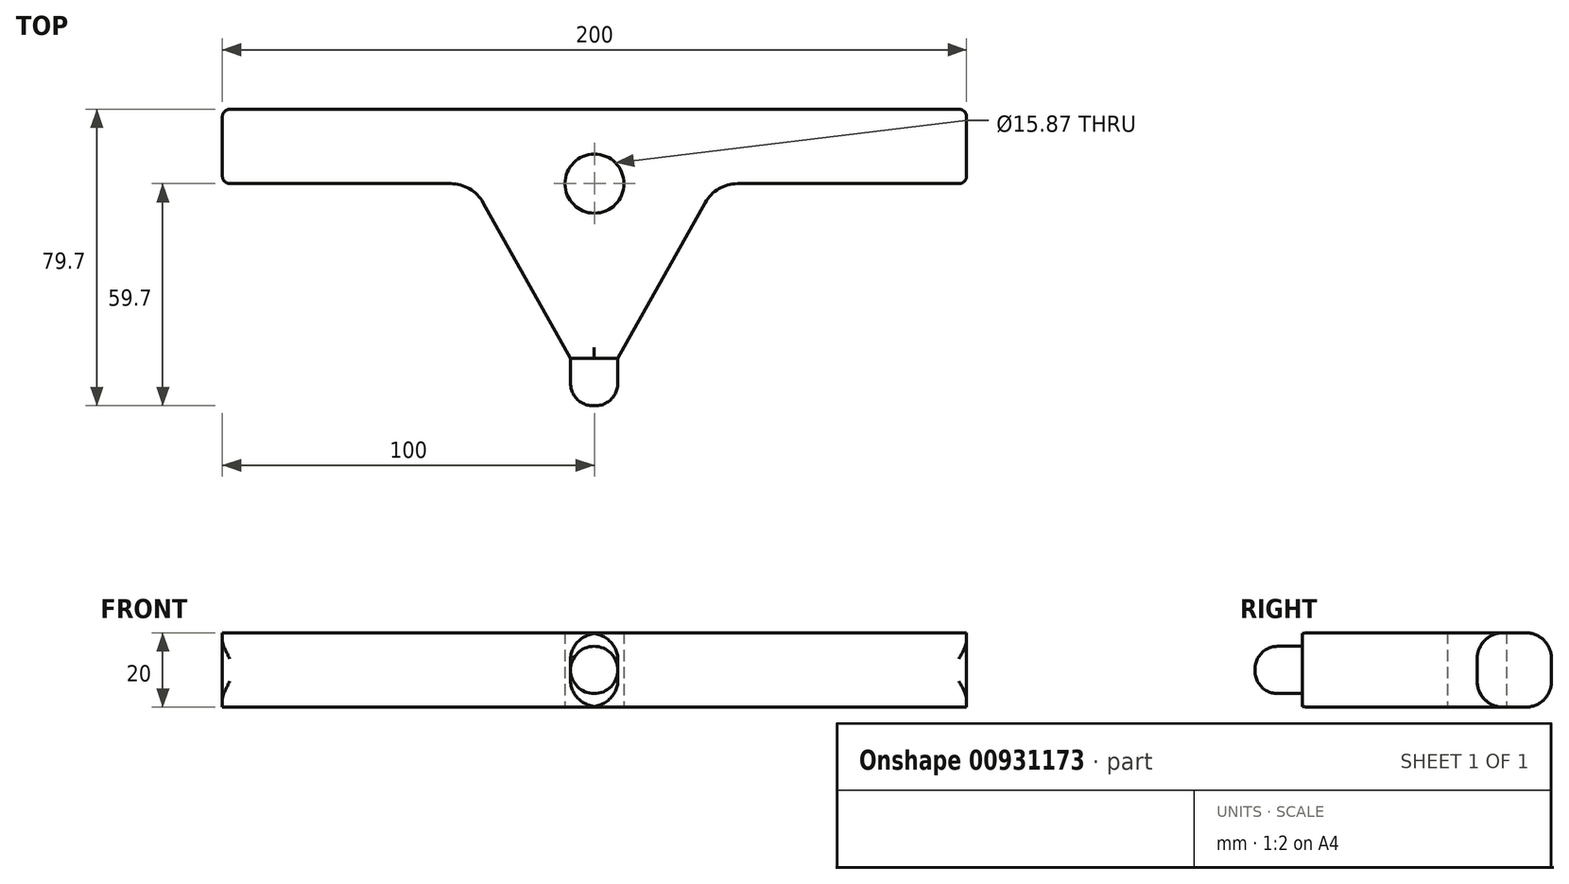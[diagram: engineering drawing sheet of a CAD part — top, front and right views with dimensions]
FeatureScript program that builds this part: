
annotation { "Feature Type Name" : "Feature", "Feature Type Description" : "" }
export const myFeature = defineFeature(function(context is Context, id is Id, definition is map)
    precondition{}
    {
        {
            var Q0;
            Q0=qCreatedBy(makeId("Top.planeOp"),FACE);
            var sketch = newSketch(context, id + "F0", { "sketchPlane" : qUnion([Q0])});
            skLineSegment(sketch, "E0.top", {"start": v(-98, 20) * mm, "end": v(98, 20) * mm});
            skLineSegment(sketch, "E0.left", {"start": v(-100, 2) * mm, "end": v(-100, 18) * mm});
            skLineSegment(sketch, "E0.right", {"start": v(100, 2) * mm, "end": v(100, 18) * mm});
            skPoint(sketch, "E1", {"position": v(0, 0) * mm});
            skPoint(sketch, "E2", {"position": v(0, 20) * mm});
            skPoint(sketch, "E3", {"position": v(-6.43, -47) * mm});
            skPoint(sketch, "E4", {"position": v(6.27, -47) * mm});
            skLineSegment(sketch, "E5.top", {"start": v(-6.43, -59.7) * mm, "end": v(6.27, -59.7) * mm});
            skLineSegment(sketch, "E5.left", {"start": v(-6.43, -47) * mm, "end": v(-6.43, -59.7) * mm});
            skLineSegment(sketch, "E5.right", {"start": v(6.27, -47) * mm, "end": v(6.27, -59.7) * mm});
            skPoint(sketch, "E6", {"position": v(-0.08, -59.7) * mm});
            skLineSegment(sketch, "E7", {"start": v(-0.08, -59.7) * mm, "end": v(0, 20) * mm, "construction": true});
            skLineSegment(sketch, "E8", {"start": v(-98, 0) * mm, "end": v(-38.63, 0) * mm});
            skLineSegment(sketch, "E9", {"start": v(98, 0) * mm, "end": v(38.47, 0) * mm});
            skPoint(sketch, "E10.visualSharp", {"position": v(100, 0) * mm});
            skArc(sketch, "E10.filletArc", {"start": v(98, 0) * mm, "mid": v(99.41, 0.59) * mm, "end": v(100, 2) * mm});
            skPoint(sketch, "E11.visualSharp", {"position": v(100, 20) * mm});
            skArc(sketch, "E11.filletArc", {"start": v(100, 18) * mm, "mid": v(99.41, 19.41) * mm, "end": v(98, 20) * mm});
            skPoint(sketch, "E12.visualSharp", {"position": v(-100, 0) * mm});
            skArc(sketch, "E12.filletArc", {"start": v(-100, 2) * mm, "mid": v(-99.41, 0.59) * mm, "end": v(-98, 0) * mm});
            skPoint(sketch, "E13.visualSharp", {"position": v(-100, 20) * mm});
            skArc(sketch, "E13.filletArc", {"start": v(-98, 20) * mm, "mid": v(-99.41, 19.41) * mm, "end": v(-100, 18) * mm});
            skLineSegment(sketch, "E14", {"start": v(6.27, -47) * mm, "end": v(29.75, -5.11) * mm});
            skPoint(sketch, "E15.visualSharp", {"position": v(32.62, 0) * mm});
            skArc(sketch, "E15.filletArc", {"start": v(38.47, 0) * mm, "mid": v(33.42, -1.37) * mm, "end": v(29.75, -5.11) * mm});
            skLineSegment(sketch, "E16", {"start": v(-6.43, -47) * mm, "end": v(-29.9, -5.11) * mm});
            skPoint(sketch, "E17.visualSharp", {"position": v(-32.77, 0) * mm});
            skArc(sketch, "E17.filletArc", {"start": v(-29.9, -5.11) * mm, "mid": v(-33.57, -1.37) * mm, "end": v(-38.63, 0) * mm});
            skCircle(sketch, "E18", {"center": v(0, 0) * mm, "radius": 7.93 * mm});
            skSolve(sketch);
        }
        {
            var Q0;
            Q0=makeQuery(id+"F0.imprint","IMPRINT",FACE,{"disambiguationData":[TD([[makeQuery(id+"F0.imprint","IMPRINT",EDGE,{"derivedFrom":sQuery(id+"F0.wireOp",EDGE,"E0.top")}),-1.0]])]});
            extrude(context, id + "F1", {"entities" : qUnion([Q0]), "depth" : 20 * mm, "offsetDistance" : 25 * mm});
        }
        {
            var Q0;
            Q0=makeQuery(id+"F1.opExtrude","SWEPT_FACE",FACE,{"disambiguationData":[OSD([sQuery(id+"F0.wireOp",EDGE,"E5.top")])]});
            extrude(context, id + "F2", {"entities" : qUnion([Q0]), "operationType" : NewBodyOperationType.REMOVE, "oppositeDirection" : true, "depth" : 12.7 * mm, "offsetDistance" : 25 * mm});
        }
        {
            var Q0;
            Q0=makeQuery(id+"F2.boolean.opBoolean","COPY",FACE,{"derivedFrom":makeQuery(id+"F2.opExtrude","CAP_FACE",FACE,{"disambiguationData":[OSD([sQuery(id+"F0.wireOp",EDGE,"E5.top")])],"isStart":false})});
            var sketch = newSketch(context, id + "F3", { "sketchPlane" : qUnion([Q0])});
            skCircle(sketch, "E19", {"center": v(-0.08, 10) * mm, "radius": 6.35 * mm});
            skSolve(sketch);
        }
        {
            var Q0;
            {var subQ0=sQuery(id+"F3.wireOp",EDGE,"E19");var subQ1=sQuery(id+"F0.wireOp",EDGE,"E5.left");var subQ2=sQuery(id+"F0.wireOp",EDGE,"E5.top");var subQ3=makeQuery(id+"F3.imprint","INTERSECT",VERTEX,{"derivedFrom":[makeQuery(id+"F2.boolean.opBoolean","MERGE",EDGE,{"derivedFrom":[makeQuery(id+"F1.opExtrude","SWEPT_EDGE",EDGE,{"disambiguationData":[OSD([subQ1,sQuery(id+"F0.wireOp",EDGE,"E16")])]})],"fromTools":[makeQuery(id+"F2.opExtrude","CAP_EDGE",EDGE,{"disambiguationData":[OSD([subQ2,subQ1])],"isStart":false})]}),subQ0]});Q0=makeQuery(id+"F3.imprint","IMPRINT",FACE,{"disambiguationData":[TD([[makeQuery(id+"F3.imprint","IMPRINT",EDGE,{"disambiguationData":[TD([[subQ3,1.0]])],"derivedFrom":subQ0}),1.0]])]});}
            extrude(context, id + "F4", {"entities" : qUnion([Q0]), "operationType" : NewBodyOperationType.ADD, "depth" : 12.7 * mm, "offsetDistance" : 25 * mm});
        }
        {
            var Q0;
            Q0=makeQuery(id+"F4.opExtrude","CAP_FACE",FACE,{"disambiguationData":[OSD([sQuery(id+"F3.wireOp",EDGE,"E19")])],"isStart":false});
            fillet(context, id + "F5", {"entities" : qUnion([Q0]), "radius" : 6.04 * mm, "allowEdgeOverflow" : false});
        }
        {
            var Q0;
            Q0=makeQuery(id+"F1.opExtrude","CAP_EDGE",EDGE,{"disambiguationData":[OSD([sQuery(id+"F0.wireOp",EDGE,"E9")])],"isStart":true});
            var Q1;
            Q1=makeQuery(id+"F1.opExtrude","CAP_EDGE",EDGE,{"disambiguationData":[OSD([sQuery(id+"F0.wireOp",EDGE,"E15.filletArc")])],"isStart":true});
            var Q2;
            Q2=makeQuery(id+"F1.opExtrude","CAP_EDGE",EDGE,{"disambiguationData":[OSD([sQuery(id+"F0.wireOp",EDGE,"E14")])],"isStart":true});
            var Q3;
            Q3=makeQuery(id+"F1.opExtrude","CAP_EDGE",EDGE,{"disambiguationData":[OSD([sQuery(id+"F0.wireOp",EDGE,"E16")])],"isStart":true});
            var Q4;
            Q4=makeQuery(id+"F1.opExtrude","CAP_EDGE",EDGE,{"disambiguationData":[OSD([sQuery(id+"F0.wireOp",EDGE,"E17.filletArc")])],"isStart":true});
            var Q5;
            Q5=makeQuery(id+"F1.opExtrude","CAP_EDGE",EDGE,{"disambiguationData":[OSD([sQuery(id+"F0.wireOp",EDGE,"E8")])],"isStart":true});
            var Q6;
            Q6=makeQuery(id+"F1.opExtrude","CAP_EDGE",EDGE,{"disambiguationData":[OSD([sQuery(id+"F0.wireOp",EDGE,"E0.top")])],"isStart":true});
            var Q7;
            Q7=makeQuery(id+"F1.opExtrude","CAP_EDGE",EDGE,{"disambiguationData":[OSD([sQuery(id+"F0.wireOp",EDGE,"E9")])],"isStart":false});
            var Q8;
            Q8=makeQuery(id+"F1.opExtrude","CAP_EDGE",EDGE,{"disambiguationData":[OSD([sQuery(id+"F0.wireOp",EDGE,"E15.filletArc")])],"isStart":false});
            var Q9;
            Q9=makeQuery(id+"F1.opExtrude","CAP_EDGE",EDGE,{"disambiguationData":[OSD([sQuery(id+"F0.wireOp",EDGE,"E14")])],"isStart":false});
            var Q10;
            Q10=makeQuery(id+"F1.opExtrude","CAP_EDGE",EDGE,{"disambiguationData":[OSD([sQuery(id+"F0.wireOp",EDGE,"E16")])],"isStart":false});
            var Q11;
            Q11=makeQuery(id+"F1.opExtrude","CAP_EDGE",EDGE,{"disambiguationData":[OSD([sQuery(id+"F0.wireOp",EDGE,"E17.filletArc")])],"isStart":false});
            var Q12;
            Q12=makeQuery(id+"F1.opExtrude","CAP_EDGE",EDGE,{"disambiguationData":[OSD([sQuery(id+"F0.wireOp",EDGE,"E8")])],"isStart":false});
            var Q13;
            Q13=makeQuery(id+"F1.opExtrude","CAP_EDGE",EDGE,{"disambiguationData":[OSD([sQuery(id+"F0.wireOp",EDGE,"E0.top")])],"isStart":false});
            fillet(context, id + "F6", {"entities" : qUnion([Q0, Q1, Q2, Q3, Q4, Q5, Q6, Q7, Q8, Q9, Q10, Q11, Q12, Q13]), "radius" : 7 * mm, "allowEdgeOverflow" : false});
        }
    });
